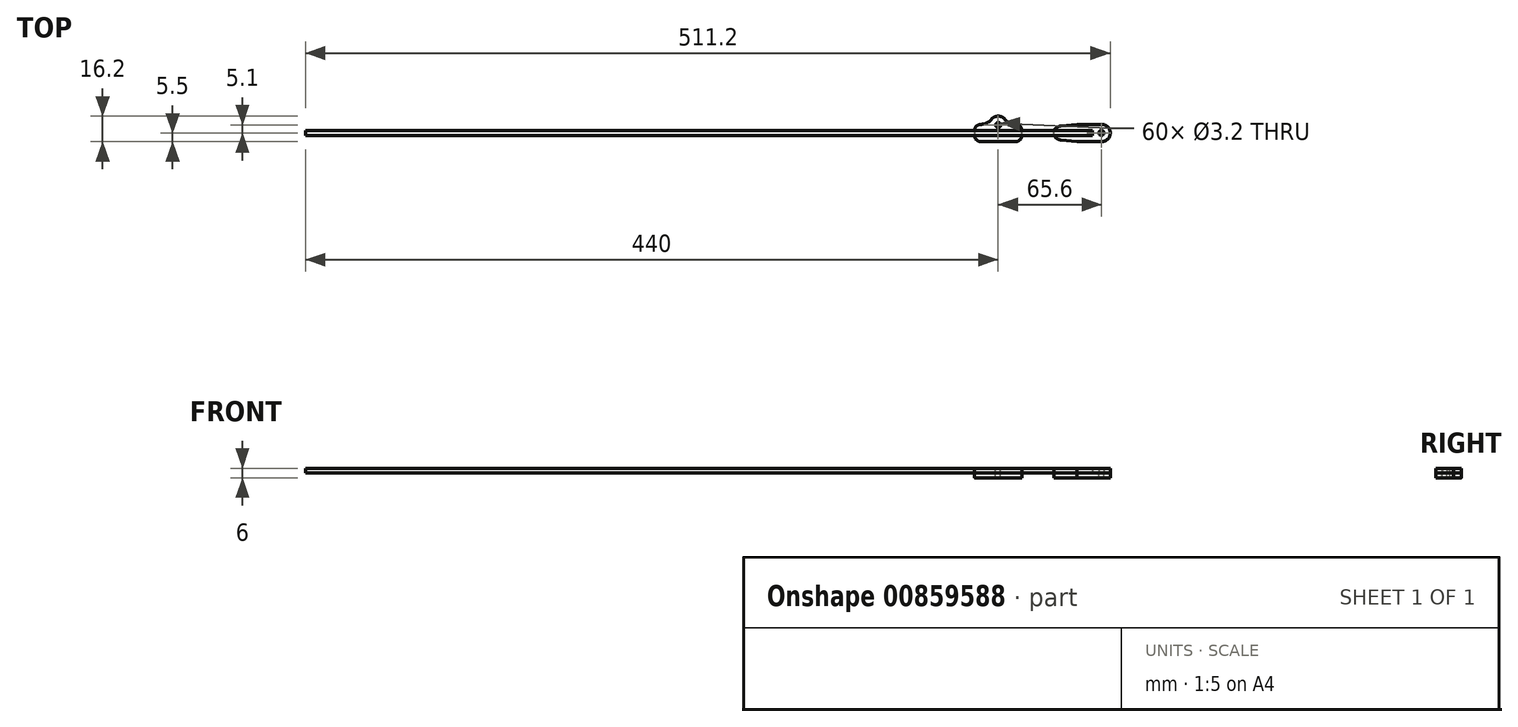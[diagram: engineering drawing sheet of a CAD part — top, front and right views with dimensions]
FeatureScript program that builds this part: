
annotation { "Feature Type Name" : "Feature", "Feature Type Description" : "" }
export const myFeature = defineFeature(function(context is Context, id is Id, definition is map)
    precondition{}
    {
        {
            var Q0;
            Q0=qCreatedBy(makeId("Top.planeOp"),FACE);
            var sketch = newSketch(context, id + "F0", { "sketchPlane" : qUnion([Q0])});
            skLineSegment(sketch, "E0.bottom", {"start": v(0, 0) * mm, "end": v(-500, 0) * mm});
            skLineSegment(sketch, "E0.top", {"start": v(0, 3) * mm, "end": v(-500, 3) * mm});
            skLineSegment(sketch, "E0.left", {"start": v(0, 0) * mm, "end": v(0, 3) * mm});
            skLineSegment(sketch, "E0.right", {"start": v(-500, 0) * mm, "end": v(-500, 3) * mm});
            skSolve(sketch);
        }
        {
            var Q0;
            Q0=makeQuery(id+"F0.imprint","IMPRINT",FACE,{"disambiguationData":[TD([[makeQuery(id+"F0.imprint","IMPRINT",EDGE,{"derivedFrom":sQuery(id+"F0.wireOp",EDGE,"E0.bottom")}),-1.0]])]});
            extrude(context, id + "F1", {"entities" : qUnion([Q0]), "depth" : 3 * mm, "offsetDistance" : 25 * mm});
        }
        {
            var Q0;
            Q0=qCreatedBy(makeId("Top.planeOp"),FACE);
            var sketch = newSketch(context, id + "F2", { "sketchPlane" : qUnion([Q0])});
            skLineSegment(sketch, "E1.0", {"start": v(0, 0) * mm, "end": v(0, 3) * mm});
            skLineSegment(sketch, "E2", {"start": v(0, 3) * mm, "end": v(-24.63, 3) * mm});
            skLineSegment(sketch, "E3", {"start": v(0, 1.5) * mm, "end": v(11.2, 1.5) * mm, "construction": true});
            skLineSegment(sketch, "E4", {"start": v(-20, 6) * mm, "end": v(-10, 7) * mm});
            skLineSegment(sketch, "E5", {"start": v(-10, 7) * mm, "end": v(0, 7) * mm});
            skArc(sketch, "E6", {"start": v(-20, 6) * mm, "mid": v(-22.68, 5.06) * mm, "end": v(-24.63, 3) * mm});
            skLineSegment(sketch, "E7", {"start": v(-10, 7) * mm, "end": v(-10, 6) * mm, "construction": true});
            skLineSegment(sketch, "E8", {"start": v(-10, 6) * mm, "end": v(-20, 6) * mm, "construction": true});
            skArc(sketch, "E9", {"start": v(4, 1.5) * mm, "mid": v(5.6, 3.1) * mm, "end": v(7.2, 1.5) * mm});
            skLineSegment(sketch, "E10", {"start": v(0, 7) * mm, "end": v(5.7, 7) * mm});
            skArc(sketch, "E11", {"start": v(11.2, 1.5) * mm, "mid": v(9.59, 5.39) * mm, "end": v(5.7, 7) * mm});
            skLineSegment(sketch, "E12.MirrorCS", {"start": v(-10, -3) * mm, "end": v(-20, -3) * mm, "construction": true});
            skLineSegment(sketch, "E13.MirrorCS", {"start": v(-10, -4) * mm, "end": v(-10, -3) * mm, "construction": true});
            skLineSegment(sketch, "E14.MirrorCS", {"start": v(-10, -4) * mm, "end": v(0, -4) * mm});
            skLineSegment(sketch, "E15.MirrorCS", {"start": v(-20, -3) * mm, "end": v(-10, -4) * mm});
            skArc(sketch, "E16.MirrorCS", {"start": v(11.2, 1.5) * mm, "mid": v(9.59, -2.39) * mm, "end": v(5.7, -4) * mm});
            skLineSegment(sketch, "E17.MirrorCS", {"start": v(0, 3) * mm, "end": v(0, 0) * mm});
            skArc(sketch, "E18.MirrorCS", {"start": v(4, 1.5) * mm, "mid": v(5.6, -0.1) * mm, "end": v(7.2, 1.5) * mm});
            skLineSegment(sketch, "E19.MirrorCS", {"start": v(0, -4) * mm, "end": v(5.7, -4) * mm});
            skLineSegment(sketch, "E20.MirrorCS", {"start": v(0, 0) * mm, "end": v(-24.63, 0) * mm});
            skArc(sketch, "E21.MirrorCS", {"start": v(-20, -3) * mm, "mid": v(-22.68, -2.06) * mm, "end": v(-24.63, 0) * mm});
            skSolve(sketch);
        }
        {
            var Q0;
            Q0=makeQuery(id+"F2.imprint","IMPRINT",FACE,{"disambiguationData":[TD([[makeQuery(id+"F2.imprint","IMPRINT",EDGE,{"derivedFrom":sQuery(id+"F2.wireOp",EDGE,"E2")}),-1.0]])]});
            var Q1;
            Q1=makeQuery(id+"F1.opExtrude","CAP_FACE",FACE,{"disambiguationData":[OSD([sQuery(id+"F0.wireOp",EDGE,"E0.bottom"),sQuery(id+"F0.wireOp",EDGE,"E0.top"),sQuery(id+"F0.wireOp",EDGE,"E0.left"),sQuery(id+"F0.wireOp",EDGE,"E0.right")])],"isStart":false});
            extrude(context, id + "F3", {"entities" : qUnion([Q0]), "endBound" : BoundingType.UP_TO_SURFACE, "depth" : 25 * mm, "endBoundEntityFace" : qUnion([Q1]), "offsetDistance" : 25 * mm});
        }
        {
            var Q0;
            Q0=makeQuery(id+"F1.opExtrude","CAP_FACE",FACE,{"disambiguationData":[OSD([sQuery(id+"F0.wireOp",EDGE,"E0.bottom"),sQuery(id+"F0.wireOp",EDGE,"E0.top"),sQuery(id+"F0.wireOp",EDGE,"E0.left"),sQuery(id+"F0.wireOp",EDGE,"E0.right")])],"isStart":true});
            var sketch = newSketch(context, id + "F4", { "sketchPlane" : qUnion([Q0])});
            skLineSegment(sketch, "E22.0.0", {"start": v(-10, 4) * mm, "end": v(-20, 3) * mm});
            skArc(sketch, "E22.0.1", {"start": v(-20, 3) * mm, "mid": v(-22.68, 2.06) * mm, "end": v(-24.63, 0) * mm});
            skArc(sketch, "E22.0.5", {"start": v(-24.63, -3) * mm, "mid": v(-22.68, -5.06) * mm, "end": v(-20, -6) * mm});
            skLineSegment(sketch, "E22.0.6", {"start": v(-20, -6) * mm, "end": v(-10, -7) * mm});
            skLineSegment(sketch, "E22.0.7", {"start": v(-10, -7) * mm, "end": v(5.7, -7) * mm});
            skArc(sketch, "E22.0.8", {"start": v(5.7, -7) * mm, "mid": v(11.2, -1.5) * mm, "end": v(5.7, 4) * mm});
            skLineSegment(sketch, "E22.0.9", {"start": v(5.7, 4) * mm, "end": v(-10, 4) * mm});
            skLineSegment(sketch, "E23", {"start": v(-24.63, 0) * mm, "end": v(-24.63, -3) * mm});
            skCircle(sketch, "E24.0", {"center": v(5.6, -1.5) * mm, "radius": 1.6 * mm});
            skSolve(sketch);
        }
        {
            var Q0;
            Q0 = qSketchRegion(id + "F4", true);
            extrude(context, id + "F5", {"entities" : qUnion([Q0]), "depth" : 3 * mm, "offsetDistance" : 25 * mm});
        }
        {
            var Q0;
            Q0=makeQuery(id+"F1.opExtrude","CAP_FACE",FACE,{"disambiguationData":[OSD([sQuery(id+"F0.wireOp",EDGE,"E0.bottom"),sQuery(id+"F0.wireOp",EDGE,"E0.top"),sQuery(id+"F0.wireOp",EDGE,"E0.left"),sQuery(id+"F0.wireOp",EDGE,"E0.right")])],"isStart":false});
            var sketch = newSketch(context, id + "F6", { "sketchPlane" : qUnion([Q0])});
            skLineSegment(sketch, "E25", {"start": v(-60, 3) * mm, "end": v(-75, 3) * mm});
            skCircle(sketch, "E26", {"center": v(-60, 6.6) * mm, "radius": 1.6 * mm});
            skArc(sketch, "E27", {"start": v(-60, 12.2) * mm, "mid": v(-62.4, 11.66) * mm, "end": v(-64.33, 10.15) * mm});
            skArc(sketch, "E28", {"start": v(-64.33, 10.15) * mm, "mid": v(-67.3, 7.83) * mm, "end": v(-71, 7) * mm});
            skArc(sketch, "E29", {"start": v(-71, 7) * mm, "mid": v(-73.83, 5.83) * mm, "end": v(-75, 3) * mm});
            skLineSegment(sketch, "E30", {"start": v(-60, 3) * mm, "end": v(-60, 12.2) * mm, "construction": true});
            skArc(sketch, "E31.MirrorCS", {"start": v(-60, 12.2) * mm, "mid": v(-57.6, 11.66) * mm, "end": v(-55.67, 10.15) * mm});
            skArc(sketch, "E32.MirrorCS", {"start": v(-55.67, 10.15) * mm, "mid": v(-52.7, 7.83) * mm, "end": v(-49, 7) * mm});
            skArc(sketch, "E33.MirrorCS", {"start": v(-49, 7) * mm, "mid": v(-46.17, 5.83) * mm, "end": v(-45, 3) * mm});
            skLineSegment(sketch, "E34.MirrorCS", {"start": v(-60, 3) * mm, "end": v(-45, 3) * mm});
            skSolve(sketch);
        }
        {
            var Q0;
            Q0=makeQuery(id+"F6.imprint","IMPRINT",FACE,{"disambiguationData":[TD([[makeQuery(id+"F6.imprint","IMPRINT",EDGE,{"derivedFrom":sQuery(id+"F6.wireOp",EDGE,"E25")}),-1.0]])]});
            var Q1;
            Q1=makeQuery(id+"F1.opExtrude","CAP_FACE",FACE,{"disambiguationData":[OSD([sQuery(id+"F0.wireOp",EDGE,"E0.bottom"),sQuery(id+"F0.wireOp",EDGE,"E0.top"),sQuery(id+"F0.wireOp",EDGE,"E0.left"),sQuery(id+"F0.wireOp",EDGE,"E0.right")])],"isStart":true});
            extrude(context, id + "F7", {"entities" : qUnion([Q0]), "endBound" : BoundingType.UP_TO_SURFACE, "oppositeDirection" : true, "depth" : 25 * mm, "endBoundEntityFace" : qUnion([Q1]), "offsetDistance" : 25 * mm});
        }
        {
            var Q0;
            Q0=makeQuery(id+"F7.opExtrude","CAP_FACE",FACE,{"disambiguationData":[OSD([sQuery(id+"F6.wireOp",EDGE,"E25"),sQuery(id+"F6.wireOp",EDGE,"E26"),sQuery(id+"F6.wireOp",EDGE,"E27"),sQuery(id+"F6.wireOp",EDGE,"E28"),sQuery(id+"F6.wireOp",EDGE,"E29"),sQuery(id+"F6.wireOp",EDGE,"E31.MirrorCS"),sQuery(id+"F6.wireOp",EDGE,"E32.MirrorCS"),sQuery(id+"F6.wireOp",EDGE,"E33.MirrorCS"),sQuery(id+"F6.wireOp",EDGE,"E34.MirrorCS")])],"isStart":false});
            var sketch = newSketch(context, id + "F8", { "sketchPlane" : qUnion([Q0])});
            skArc(sketch, "E35.0.1", {"start": v(-75, -3) * mm, "mid": v(-73.83, -5.83) * mm, "end": v(-71, -7) * mm});
            skArc(sketch, "E35.0.2", {"start": v(-71, -7) * mm, "mid": v(-67.3, -7.83) * mm, "end": v(-64.33, -10.15) * mm});
            skArc(sketch, "E35.0.3", {"start": v(-64.33, -10.15) * mm, "mid": v(-60, -12.2) * mm, "end": v(-55.67, -10.15) * mm});
            skArc(sketch, "E35.0.4", {"start": v(-49, -7) * mm, "mid": v(-52.7, -7.83) * mm, "end": v(-55.67, -10.15) * mm});
            skArc(sketch, "E35.0.5", {"start": v(-49, -7) * mm, "mid": v(-46.17, -5.83) * mm, "end": v(-45, -3) * mm});
            skLineSegment(sketch, "E36", {"start": v(-75, -3) * mm, "end": v(-75, 0) * mm});
            skLineSegment(sketch, "E37", {"start": v(-71, 4) * mm, "end": v(-49, 4) * mm});
            skLineSegment(sketch, "E38", {"start": v(-45, 0) * mm, "end": v(-45, -3) * mm});
            skCircle(sketch, "E39.0", {"center": v(-60, -6.6) * mm, "radius": 1.6 * mm});
            skPoint(sketch, "E40.visualSharp", {"position": v(-75, 4) * mm});
            skArc(sketch, "E40.filletArc", {"start": v(-71, 4) * mm, "mid": v(-73.83, 2.83) * mm, "end": v(-75, 0) * mm});
            skPoint(sketch, "E41.visualSharp", {"position": v(-45, 4) * mm});
            skArc(sketch, "E41.filletArc", {"start": v(-45, 0) * mm, "mid": v(-46.17, 2.83) * mm, "end": v(-49, 4) * mm});
            skSolve(sketch);
        }
        {
            var Q0;
            Q0 = qSketchRegion(id + "F8", true);
            extrude(context, id + "F9", {"entities" : qUnion([Q0]), "depth" : 3 * mm, "offsetDistance" : 25 * mm});
        }
        {
            var Q0;
            Q0=makeQuery(id+"F9.opExtrude","CAP_FACE",FACE,{"disambiguationData":[OSD([sQuery(id+"F8.wireOp",EDGE,"E35.0.1"),sQuery(id+"F8.wireOp",EDGE,"E35.0.2"),sQuery(id+"F8.wireOp",EDGE,"E35.0.3"),sQuery(id+"F8.wireOp",EDGE,"E35.0.4"),sQuery(id+"F8.wireOp",EDGE,"E35.0.5"),sQuery(id+"F8.wireOp",EDGE,"E36"),sQuery(id+"F8.wireOp",EDGE,"E37"),sQuery(id+"F8.wireOp",EDGE,"E38"),sQuery(id+"F8.wireOp",EDGE,"E39.0"),sQuery(id+"F8.wireOp",EDGE,"E40.filletArc"),sQuery(id+"F8.wireOp",EDGE,"E41.filletArc")])],"isStart":true});
            var sketch = newSketch(context, id + "F10", { "sketchPlane" : qUnion([Q0])});
            skLineSegment(sketch, "E42.1", {"start": v(0, 0) * mm, "end": v(-500, 0) * mm});
            skSolve(sketch);
        }
        {
            var Q0;
            Q0=makeQuery(id+"F10.imprint","IMPRINT",FACE,{"disambiguationData":[TD([[makeQuery(id+"F10.imprint","IMPRINT",EDGE,{"derivedFrom":makeQuery(id+"F9.opExtrude","CAP_EDGE",EDGE,{"disambiguationData":[OSD([sQuery(id+"F8.wireOp",EDGE,"E37")])],"isStart":true})}),1.0]])]});
            var Q1;
            Q1=makeQuery(id+"F1.opExtrude","CAP_FACE",FACE,{"disambiguationData":[OSD([sQuery(id+"F0.wireOp",EDGE,"E0.bottom"),sQuery(id+"F0.wireOp",EDGE,"E0.top"),sQuery(id+"F0.wireOp",EDGE,"E0.left"),sQuery(id+"F0.wireOp",EDGE,"E0.right")])],"isStart":false});
            extrude(context, id + "F11", {"entities" : qUnion([Q0]), "endBound" : BoundingType.UP_TO_SURFACE, "depth" : 25 * mm, "endBoundEntityFace" : qUnion([Q1]), "offsetDistance" : 25 * mm});
        }
    });
